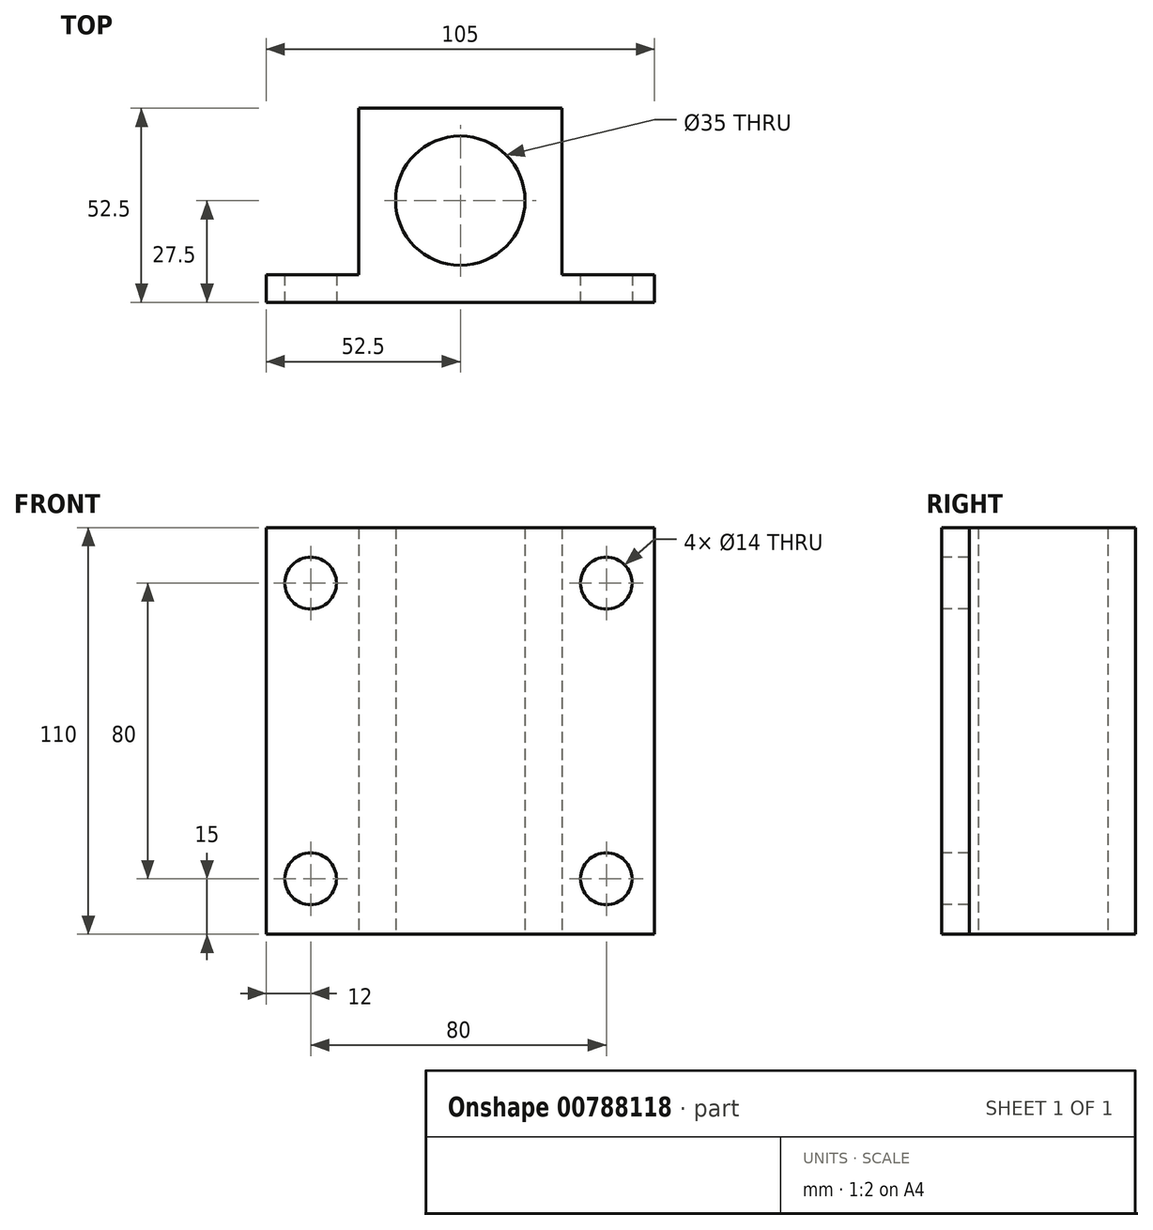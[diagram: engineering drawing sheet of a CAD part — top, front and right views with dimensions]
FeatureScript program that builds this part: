
annotation { "Feature Type Name" : "Feature", "Feature Type Description" : "" }
export const myFeature = defineFeature(function(context is Context, id is Id, definition is map)
    precondition{}
    {
        {
            var Q0;
            Q0=qCreatedBy(makeId("Top.planeOp"),FACE);
            var sketch = newSketch(context, id + "F0", { "sketchPlane" : qUnion([Q0])});
            skLineSegment(sketch, "E0", {"start": v(-52.5, 0) * mm, "end": v(-52.5, 7.5) * mm});
            skLineSegment(sketch, "E1", {"start": v(-52.5, 7.5) * mm, "end": v(-27.5, 7.5) * mm});
            skLineSegment(sketch, "E2", {"start": v(-27.5, 7.5) * mm, "end": v(-27.5, 52.5) * mm});
            skLineSegment(sketch, "E3", {"start": v(-27.5, 52.5) * mm, "end": v(0, 52.5) * mm});
            skLineSegment(sketch, "E4", {"start": v(0, 0) * mm, "end": v(-52.5, 0) * mm});
            skLineSegment(sketch, "E5", {"start": v(-40, 47.03) * mm, "end": v(-40, -43.68) * mm, "construction": true});
            skPoint(sketch, "E6", {"position": v(-40, 7.5) * mm});
            skLineSegment(sketch, "E7", {"start": v(0, 75.04) * mm, "end": v(0, -41.72) * mm, "construction": true});
            skLineSegment(sketch, "E8.MirrorCS", {"start": v(27.5, 52.5) * mm, "end": v(0, 52.5) * mm});
            skLineSegment(sketch, "E9.MirrorCS", {"start": v(27.5, 7.5) * mm, "end": v(27.5, 52.5) * mm});
            skLineSegment(sketch, "E10.MirrorCS", {"start": v(52.5, 7.5) * mm, "end": v(27.5, 7.5) * mm});
            skLineSegment(sketch, "E11.MirrorCS", {"start": v(52.5, 0) * mm, "end": v(52.5, 7.5) * mm});
            skLineSegment(sketch, "E12.MirrorCS", {"start": v(0, 0) * mm, "end": v(52.5, 0) * mm});
            skCircle(sketch, "E13", {"center": v(0, 27.5) * mm, "radius": 17.5 * mm});
            skSolve(sketch);
        }
        {
            var Q0;
            Q0 = qSketchRegion(id + "F0", true);
            extrude(context, id + "F1", {"entities" : qUnion([Q0]), "depth" : 110 * mm, "offsetDistance" : 25 * mm});
        }
        {
            var Q0;
            Q0=makeQuery(id+"F1.opExtrude","SWEPT_FACE",FACE,{"disambiguationData":[OSD([sQuery(id+"F0.wireOp",EDGE,"E4"),sQuery(id+"F0.wireOp",EDGE,"E12.MirrorCS")])]});
            var sketch = newSketch(context, id + "F2", { "sketchPlane" : qUnion([Q0])});
            skCircle(sketch, "E14", {"center": v(-40.5, 95) * mm, "radius": 7 * mm});
            skCircle(sketch, "E15", {"center": v(39.5, 95) * mm, "radius": 7 * mm});
            skCircle(sketch, "E16", {"center": v(-40.5, 15) * mm, "radius": 7 * mm});
            skCircle(sketch, "E17", {"center": v(39.5, 15) * mm, "radius": 7 * mm});
            skSolve(sketch);
        }
        {
            var Q0;
            Q0 = qSketchRegion(id + "F2", true);
            extrude(context, id + "F3", {"entities" : qUnion([Q0]), "operationType" : NewBodyOperationType.REMOVE, "oppositeDirection" : true, "depth" : 25 * mm, "offsetDistance" : 25 * mm});
        }
    });
